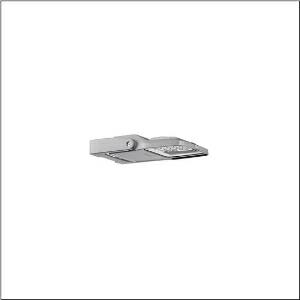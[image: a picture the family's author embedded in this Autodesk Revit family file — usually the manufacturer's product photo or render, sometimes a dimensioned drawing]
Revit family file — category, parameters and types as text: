
# Revit family: floodlight_fl_21_iq_micro___pl43_5xa7761a4a2a_9599
name_source: partatom
category: Lighting Fixtures
units: mm (PartAtom-declared; Revit-internal decimal feet)

## family parameters
Cut with Voids When Loaded = No
Host = Face
Light Source = No
Part Type = Normal
Room Calculation Point = No
Round Connector Dimension = Use Diameter
Shared = No

## types (1)
- --- (1 x LED, 3170 lm, 23.1 W, 4000K)
    Apparent Load = 23 VA
    CIE Flux Codes = 29 80 99 100 100
    Color Rendering = 70
    Color Temperature = 4000K
    Default Elevation = 1800 mm
    Description = Floodlight FL 21 iQ micro, floodlight, primary light control with lens, of PMMA, primary optical cover: protective disc, of toughened safety glass, transparent, light distribution: PL43, light emission: direct distribution, installation type: surface-mounted, LED, High Power LED, rated luminous flux: 3.170lm, luminous efficacy: 137lm/W, light colour: 740, colour temperature: 4000K, control gear: iQ Comfort/DALI, control: optimised constant luminous flux control (CLO 2.0), Desk-Remote (wireless, voltage-free reading and setting of iQ features in the workshop via application-optimized NFC function/RFID function), Light-Fading, Smart-Wire, Night-Set, Lumen-Switch, Temp-Guard, Auto-Match, with terminal, 6-pole, mains connection: 220..240V, AC, 50/60Hz, start of lifetime: 23W, end of service life: 24W, reduction: 11W, luminaire housing, of diecast aluminium, powder-coated, Siteco® metallic grey (DB 702S), corrosivity category C5 mid according to DIN EN ISO 12944, suitable for swimming pools, chlorine-resistant, sealing non-destructively replaceable, design bracket, of diecast aluminium, powder-coated, Siteco® metallic grey (DB 702S), protection rating (complete): IP66, insulation class (complete): insulation class II (safety insulation), certification: CE, ENEC, VDE, protection symbol: D, impact resistance: IK07, permissible operating ambient temperature: -40..+40°C, permissible operating ambient temperature for outdoor applications: -40..+50°C, standard: DIN EN 12944, LABS conformity tested according to VDMA 24364:2018-05, packaging unit: 1 piece

Light Distribution: PL43
    Height = 65 mm
    Lamp = 1 x LED
    Lamp Light Flux = 3170 lm
    Lamp Power = 23.1 W
    Lamp count = 1
    Length = 312 mm
    Luminous efficacy = 137 lm/W
    Manufacturer = Siteco
    ModVariant = No
    Model = 5XA7761A4A2A
    Mounting Place = Wall
    Mounting Type = Surface mounted
    Number of Poles = 1
    OnlyDefault = Yes
    Power Factor = 1
    Product Name = Floodlight FL 21 iQ micro | PL43
    Product group = floodlight | wall mounted
    ProductGroupID = 2001
    Protection Class = Protection class II
    Protection Degree = IP 66
    RLX_Detail_Level = 1
    RLX_Emergency_Light_Flux = 0 lm
    RLX_Emergency_Type = 0
    RLX_Emergency_Type_DB = No
    RlxData = <blob elided: 97685 chars, md5=0938b9c5>
    Socket = socket
    Standby Power = 0 W
    System Light Flux = 3170 lm
    System Power = 23 W
    Type Comments = factory setting: luminous flux: 100 % | dim-lin: 254 | 455 mA
    Type Image = l_1006878.jpg
    URL = http://relux.com
    VarID = @adj_198229
    Voltage = 0 V
    Weight = 0.00 kg
    Width = 230 mm

## geometry (parser evidence)
native form markers: Blend x4, Sweep x16
no freeform markers — native parametric forms only
